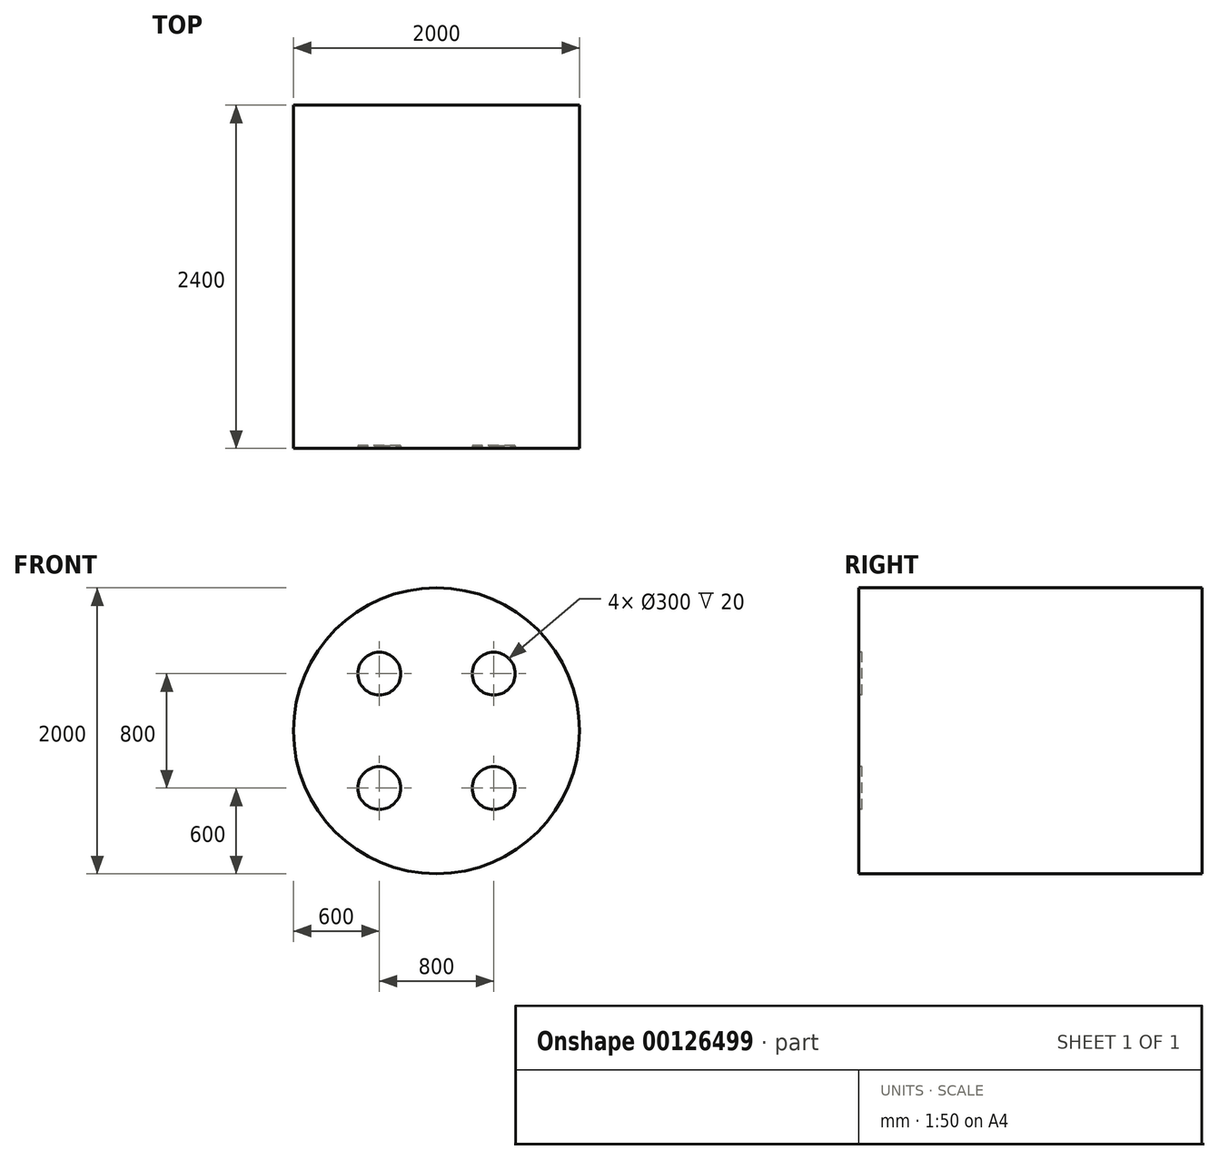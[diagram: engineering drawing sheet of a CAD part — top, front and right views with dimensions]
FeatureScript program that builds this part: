
annotation { "Feature Type Name" : "Feature", "Feature Type Description" : "" }
export const myFeature = defineFeature(function(context is Context, id is Id, definition is map)
    precondition{}
    {
        {
            var Q0;
            Q0=qCreatedBy(makeId("Front.planeOp"),FACE);
            var sketch = newSketch(context, id + "F0", { "sketchPlane" : qUnion([Q0])});
            skLineSegment(sketch, "E0", {"start": v(0, 694.2) * mm, "end": v(0, -735.04) * mm, "construction": true});
            skLineSegment(sketch, "E1", {"start": v(-1071.28, 0) * mm, "end": v(1006.16, 0) * mm, "construction": true});
            skCircle(sketch, "E2", {"center": v(0, 0) * mm, "radius": 1000 * mm});
            skSolve(sketch);
        }
        {
            var Q0;
            Q0 = qSketchRegion(id + "F0", true);
            extrude(context, id + "F1", {"entities" : qUnion([Q0]), "oppositeDirection" : true, "depth" : 2400 * mm});
        }
        {
            var Q0;
            Q0=makeQuery(id+"F1.opExtrude","CAP_FACE",FACE,{"disambiguationData":[OSD([sQuery(id+"F0.wireOp",EDGE,"E2")])],"isStart":true});
            var sketch = newSketch(context, id + "F2", { "sketchPlane" : qUnion([Q0])});
            skLineSegment(sketch, "E3", {"start": v(-1713.62, 0) * mm, "end": v(2054.63, 0) * mm, "construction": true});
            skLineSegment(sketch, "E4", {"start": v(0, -1617.72) * mm, "end": v(0, 1675.94) * mm, "construction": true});
            skCircle(sketch, "E5", {"center": v(-400, 400) * mm, "radius": 150 * mm});
            skCircle(sketch, "E6.0.1.0", {"center": v(-400, -400) * mm, "radius": 150 * mm});
            skCircle(sketch, "E6.1.0.0", {"center": v(400, 400) * mm, "radius": 150 * mm});
            skCircle(sketch, "E6.1.1.0", {"center": v(400, -400) * mm, "radius": 150 * mm});
            skLineSegment(sketch, "E6.direction1", {"start": v(-400, 400) * mm, "end": v(400, 400) * mm, "construction": true});
            skLineSegment(sketch, "E6.direction2", {"start": v(-400, 400) * mm, "end": v(-400, -400) * mm, "construction": true});
            skSolve(sketch);
        }
        {
            var Q0;
            Q0 = qSketchRegion(id + "F2", true);
            extrude(context, id + "F3", {"entities" : qUnion([Q0]), "operationType" : NewBodyOperationType.REMOVE, "oppositeDirection" : true, "depth" : 20 * mm});
        }
    });
